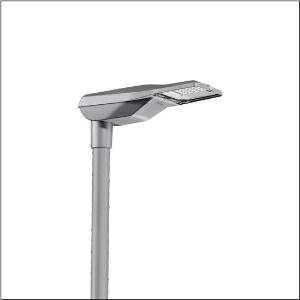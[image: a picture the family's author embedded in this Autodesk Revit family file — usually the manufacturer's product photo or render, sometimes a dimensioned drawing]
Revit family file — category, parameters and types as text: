
# Revit family: streetlight_sl_21_iq_micro___st1_0a_5xe1d41d08cb_ed56
name_source: partatom
category: Lighting Fixtures
units: mm (PartAtom-declared; Revit-internal decimal feet)

## family parameters
Cut with Voids When Loaded = No
Host = Face
Light Source = No
Part Type = Normal
Room Calculation Point = No
Round Connector Dimension = Use Diameter
Shared = No

## types (1)
- --- (1 x LED, 2980 lm, 19.4 W, 4000K)
    Apparent Load = 19 VA
    CIE Flux Codes = 37 72 97 100 100
    Color Rendering = 70
    Color Temperature = 4000K
    Default Elevation = 1800 mm
    Description = Streetlight SL 21 iQ micro, mast luminaire, primary light control with lens, of PMMA, primary optical cover: cover, of toughened safety glass, transparent, light distribution: ST1.0a, light emission: direct distribution, primary light characteristic: asymmetric, installation type: post-top, side-entry, LED, High Power LED, rated luminous flux: 2.980lm, luminous efficacy: 154lm/W, light colour: 740, colour temperature: 4000K, control: Auto-Match, Temp-Guard, Lumen-Switch, Night-Set, Smart-Wire, Light-Fading, Desk-Remote (wireless, voltage-free reading and setting of iQ features in the workshop via application-optimized NFC function/RFID function), optimised constant luminous flux control (CLO 2.0), presetting dimming linear, mains connection: 220..240V, AC, 50/60Hz, start of lifetime: 19W, end of service life: 20W, reduction: 10W, luminaire housing, of diecast aluminium, powder-coated, Siteco® metallic grey (DB 702S), corrosivity category C5 mid according to DIN EN ISO 12944, please order mast flange separately, inclination adjustable: 0°, 5°, 10°, 15°, sealing non-destructively replaceable, multi-level sealing system, length: 528mm, width: 235mm, height: 110mm, mast flange for spigot size: 42mm (side-entry): 5XC10008XM4, 60/48mm (side-entry/post-top): 5XC10108XM2, 76/60mm (side-entry/post-top): 5XC10108XM1, protection rating (complete): IP66, insulation class (complete): insulation class II (safety insulation), certification: CE, ENEC, ENEC+, VDE, impact resistance: IK09, permissible operating ambient temperature for outdoor applications: -40..+50°C, standard-compliant lighting for roads and squares, packaging unit: 1 piece

Light Distribution: ST1.0a
    Height = 110 mm
    Lamp = 1 x LED
    Lamp Light Flux = 2980 lm
    Lamp Power = 19.4 W
    Lamp count = 1
    Length = 528 mm
    Luminous efficacy = 154 lm/W
    Manufacturer = Siteco
    ModVariant = No
    Model = 5XE1D41D08CB
    Number of Poles = 1
    OnlyDefault = Yes
    Power Factor = 1
    Product Name = Streetlight SL 21 iQ micro | ST1.0a
    Product group = mast luminaire | pylon top
    ProductGroupID = 6100
    Protection Class = Protection class II
    Protection Degree = IP 66
    RLX_Detail_Level = 1
    RLX_Emergency_Light_Flux = 0 lm
    RLX_Emergency_Type = 0
    RLX_Emergency_Type_DB = No
    RlxData = <blob elided: 98661 chars, md5=f6d5bd3c>
    Socket = socket
    Standby Power = 0 W
    System Light Flux = 2980 lm
    System Power = 19 W
    Type Comments = factory setting: luminous flux: 100 % | dim-lin: 254 | 387 mA
    Type Image = l_1006881.jpg
    URL = http://relux.com
    VarID = @adj_070541
    Voltage = 0 V
    Weight = 0.00 kg
    Width = 235 mm

## geometry (parser evidence)
native form markers: Blend x4, Sweep x11
no freeform markers — native parametric forms only
